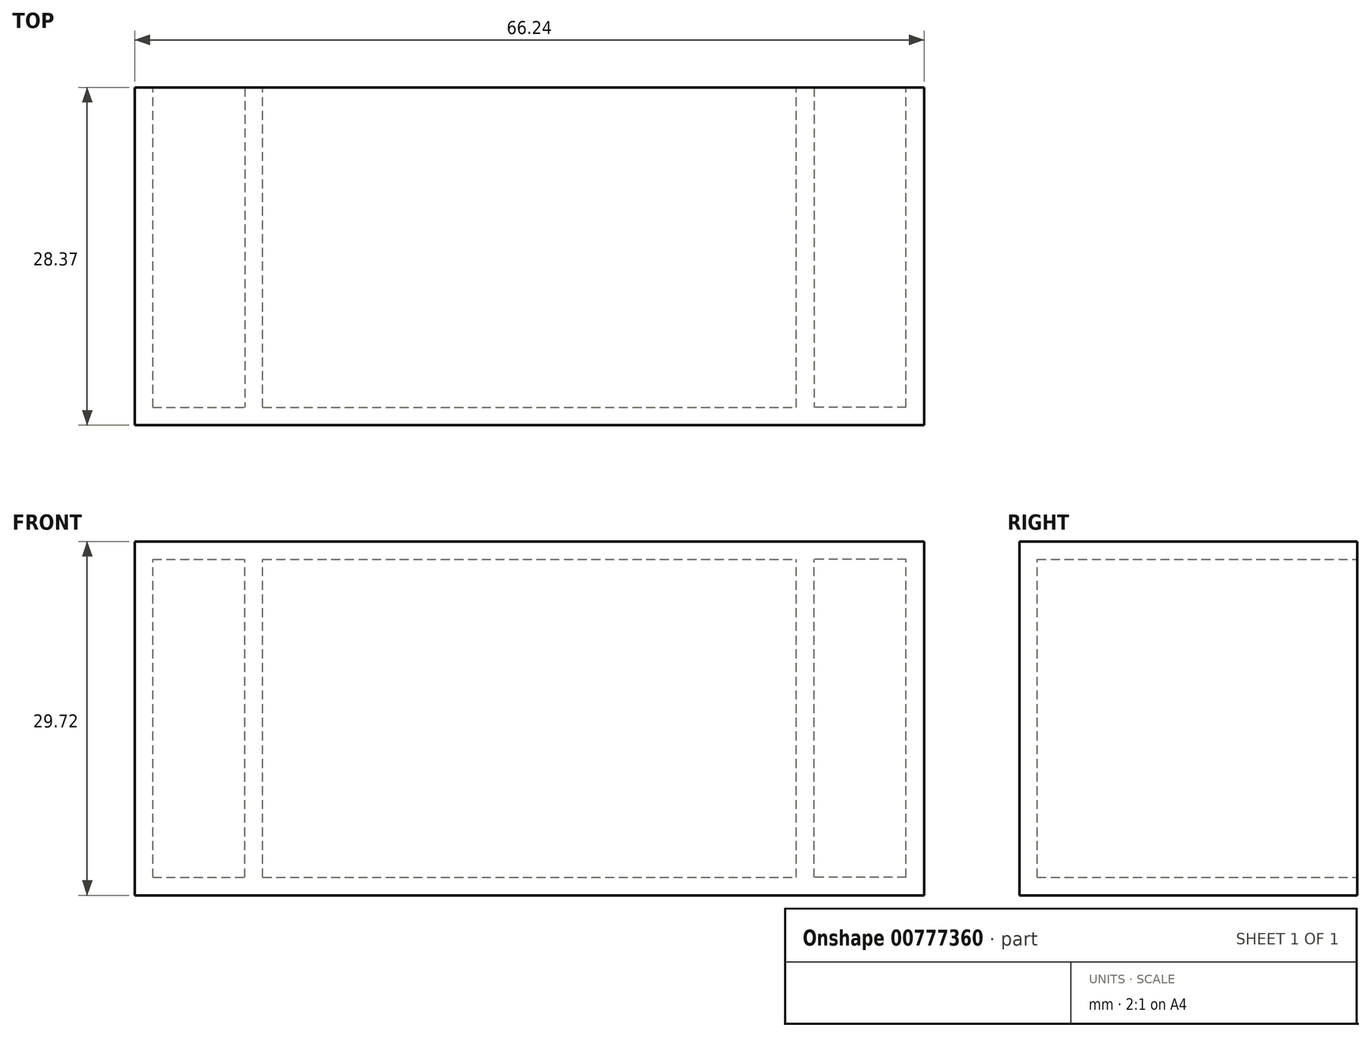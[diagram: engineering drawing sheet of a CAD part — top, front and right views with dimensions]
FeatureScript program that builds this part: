
annotation { "Feature Type Name" : "Feature", "Feature Type Description" : "" }
export const myFeature = defineFeature(function(context is Context, id is Id, definition is map)
    precondition{}
    {
        {
            var Q0;
            Q0=qCreatedBy(makeId("Top.planeOp"),FACE);
            var sketch = newSketch(context, id + "F0", { "sketchPlane" : qUnion([Q0])});
            skLineSegment(sketch, "E0.bottom", {"start": v(-33.12, 0) * mm, "end": v(23.9, 0) * mm});
            skLineSegment(sketch, "E0.top", {"start": v(-33.12, 28.37) * mm, "end": v(23.9, 28.37) * mm});
            skLineSegment(sketch, "E0.left", {"start": v(-33.12, 0) * mm, "end": v(-33.12, 28.37) * mm});
            skLineSegment(sketch, "E0.right", {"start": v(23.9, 0) * mm, "end": v(23.9, 28.37) * mm});
            skSolve(sketch);
        }
        {
            var Q0;
            Q0=makeQuery(id+"F0.imprint","IMPRINT",FACE,{"disambiguationData":[TD([[makeQuery(id+"F0.imprint","IMPRINT",EDGE,{"derivedFrom":sQuery(id+"F0.wireOp",EDGE,"E0.bottom")}),1.0]])]});
            extrude(context, id + "F1", {"entities" : qUnion([Q0]), "oppositeDirection" : true, "depth" : 29.72 * mm, "offsetDistance" : 25.4 * mm});
        }
        {
            var Q0;
            Q0=makeQuery(id+"F1.opExtrude","SWEPT_FACE",FACE,{"disambiguationData":[OSD([sQuery(id+"F0.wireOp",EDGE,"E0.top")])]});
            shell(context, id + "F2", {"entities" : qUnion([Q0]), "thickness" : 1.5 * mm});
        }
        {
            var Q0;
            Q0=makeQuery(id+"F1.opExtrude","SWEPT_BODY",BODY,{"disambiguationData":[OSD([sQuery(id+"F0.wireOp",EDGE,"E0.bottom"),sQuery(id+"F0.wireOp",EDGE,"E0.top"),sQuery(id+"F0.wireOp",EDGE,"E0.left"),sQuery(id+"F0.wireOp",EDGE,"E0.right")])]});
            var Q1;
            Q1=qCreatedBy(makeId("Right.planeOp"),FACE);
            mirror(context, id + "F3", {"operationType" : NewBodyOperationType.ADD, "entities" : qUnion([Q0]), "mirrorPlane" : qUnion([Q1])});
        }
    });
